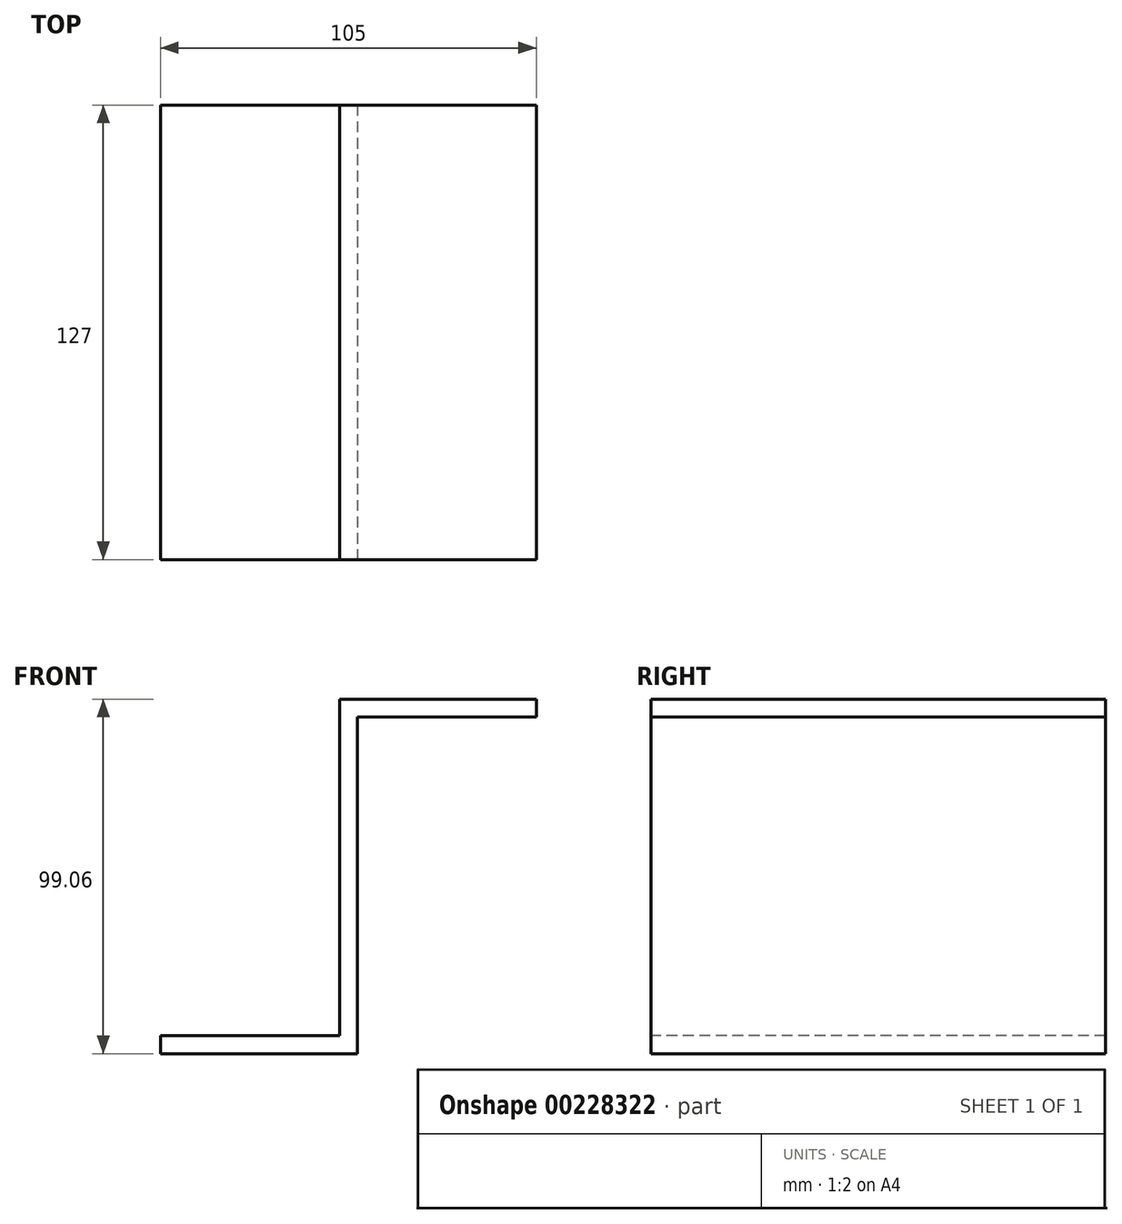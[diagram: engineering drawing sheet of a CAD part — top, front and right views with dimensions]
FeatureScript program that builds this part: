
annotation { "Feature Type Name" : "Feature", "Feature Type Description" : "" }
export const myFeature = defineFeature(function(context is Context, id is Id, definition is map)
    precondition{}
    {
        {
            var Q0;
            Q0=qCreatedBy(makeId("Front.planeOp"),FACE);
            var sketch = newSketch(context, id + "F0", { "sketchPlane" : qUnion([Q0])});
            skLineSegment(sketch, "E0.bottom", {"start": v(2.5, -49.53) * mm, "end": v(-2.5, -49.53) * mm});
            skLineSegment(sketch, "E0.top", {"start": v(2.5, 49.53) * mm, "end": v(-2.5, 49.53) * mm});
            skLineSegment(sketch, "E0.left", {"start": v(2.5, -49.53) * mm, "end": v(2.5, 49.53) * mm});
            skLineSegment(sketch, "E0.right", {"start": v(-2.5, -49.53) * mm, "end": v(-2.5, 49.53) * mm});
            skPoint(sketch, "E0.middle", {"position": v(0, 0) * mm});
            skLineSegment(sketch, "E1.bottom", {"start": v(2.5, 49.53) * mm, "end": v(52.5, 49.53) * mm});
            skLineSegment(sketch, "E1.top", {"start": v(2.5, 44.53) * mm, "end": v(52.5, 44.53) * mm});
            skLineSegment(sketch, "E1.left", {"start": v(2.5, 49.53) * mm, "end": v(2.5, 44.53) * mm});
            skLineSegment(sketch, "E1.right", {"start": v(52.5, 49.53) * mm, "end": v(52.5, 44.53) * mm});
            skLineSegment(sketch, "E2.bottom", {"start": v(-2.5, -49.53) * mm, "end": v(-52.5, -49.53) * mm});
            skLineSegment(sketch, "E2.top", {"start": v(-2.5, -44.53) * mm, "end": v(-52.5, -44.53) * mm});
            skLineSegment(sketch, "E2.left", {"start": v(-2.5, -49.53) * mm, "end": v(-2.5, -44.53) * mm});
            skLineSegment(sketch, "E2.right", {"start": v(-52.5, -49.53) * mm, "end": v(-52.5, -44.53) * mm});
            skSolve(sketch);
        }
        {
            var Q0;
            Q0=makeQuery(id+"F0.imprint","IMPRINT",FACE,{"disambiguationData":[TD([[makeQuery(id+"F0.imprint","IMPRINT",EDGE,{"derivedFrom":sQuery(id+"F0.wireOp",EDGE,"E0.bottom")}),-1.0]])]});
            var Q1;
            Q1=makeQuery(id+"F0.imprint","IMPRINT",FACE,{"disambiguationData":[TD([[makeQuery(id+"F0.imprint","IMPRINT",EDGE,{"derivedFrom":sQuery(id+"F0.wireOp",EDGE,"E1.bottom")}),-1.0]])]});
            var Q2;
            Q2=makeQuery(id+"F0.imprint","IMPRINT",FACE,{"disambiguationData":[TD([[makeQuery(id+"F0.imprint","IMPRINT",EDGE,{"derivedFrom":sQuery(id+"F0.wireOp",EDGE,"E2.bottom")}),-1.0]])]});
            extrude(context, id + "F1", {"entities" : qUnion([Q0, Q1, Q2]), "endBound" : BoundingType.SYMMETRIC, "oppositeDirection" : true, "depth" : 127 * mm});
        }
    });
